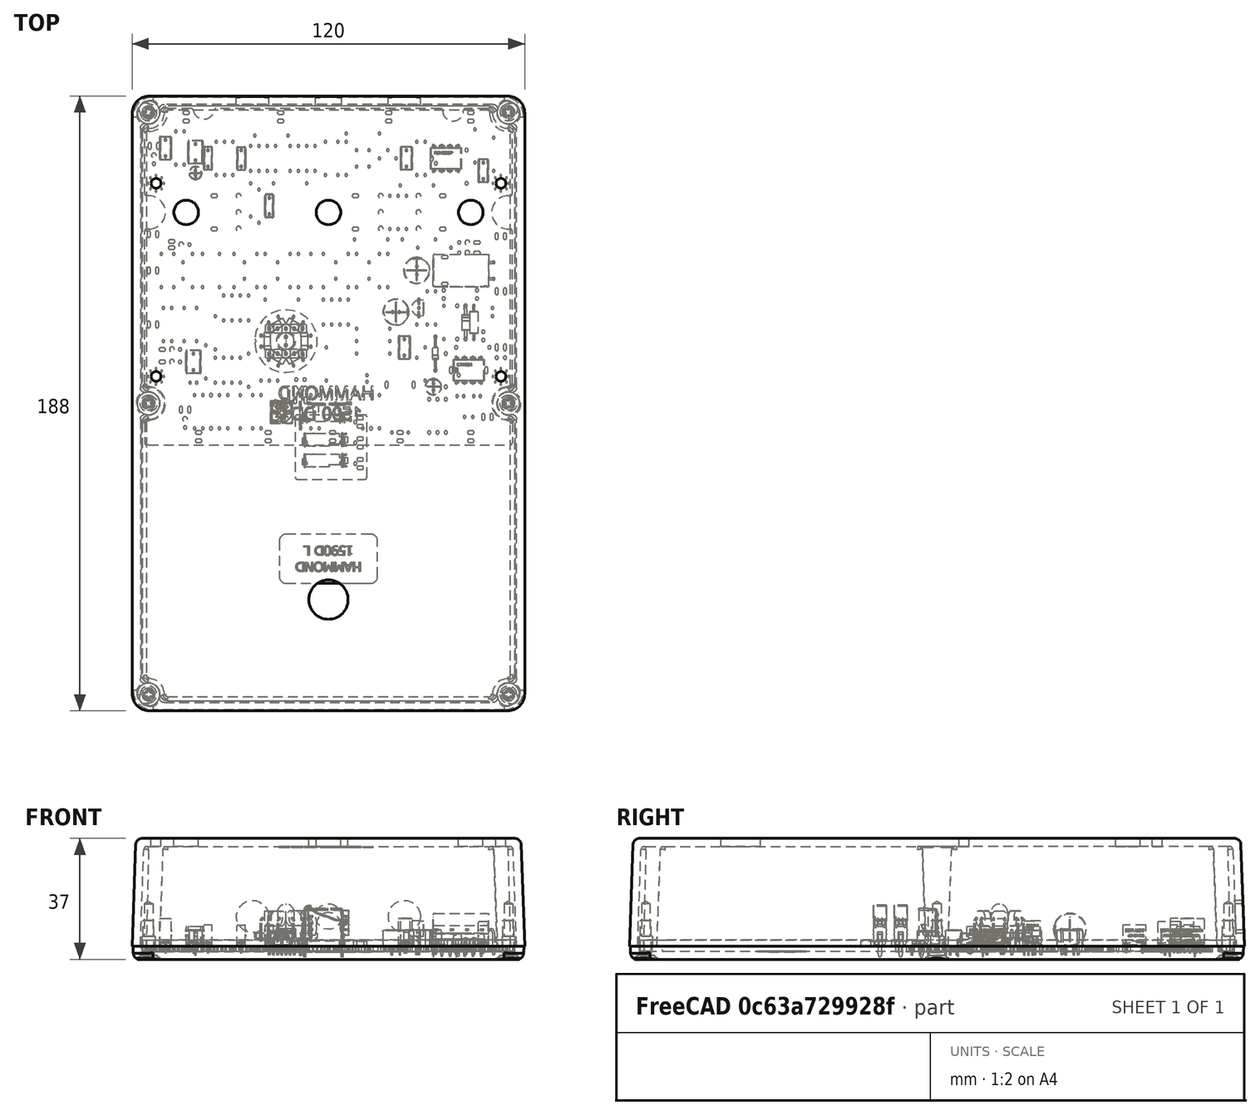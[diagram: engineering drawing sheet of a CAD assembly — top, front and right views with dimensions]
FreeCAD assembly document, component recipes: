
FREECAD ASSEMBLY — COMPONENT RECIPES ("#000-000 - Mu-Tron Phasor II - ASM3")

This assembly document has 7 components, labeled P0..P6 below (a component is one placed body or linked part). 2 of them carry a construction recipe — the FreeCAD feature program that regenerates the part from scratch, quoted from this document or its linked companion documents; the rest are supplied as boundary geometry only. No exploded tour is included for this assembly.
COMPONENT P0 — geometry summary ("#110-000-S1A - Phasor PCB"; no construction recipe available for this part):
  bounding box: 145.4 x 142.2 x 16.1 mm
  tessellated surface: 227,022 triangles
  volume: 29561 mm^3 (9% of its bounding box)
COMPONENT P1 — recipe-attached ("Hex_Spacer_FF_M3x12_FF4.008", modeled in this document).
Construction recipe (the document's own serialized feature program — sketch geometry with constraints, then the solid features built on it; lengths are millimeters unless a unit is written):

FEATURE [Sketcher::SketchObject] Sketch
  MapMode = 5
  Support = -> [XY_Plane005]
  sketch-geometry (7):
    g0: LineSegment StartX=2.35 StartY=1.35677 StartZ=0 EndX=0 EndY=2.71355 EndZ=0
    g1: LineSegment StartX=0 StartY=2.71355 StartZ=0 EndX=-2.35 EndY=1.35677 EndZ=0
    g2: LineSegment StartX=-2.35 StartY=1.35677 StartZ=0 EndX=-2.35 EndY=-1.35677 EndZ=0
    g3: LineSegment StartX=-2.35 StartY=-1.35677 StartZ=0 EndX=-2.2e-15 EndY=-2.71355 EndZ=0
    g4: LineSegment StartX=-2.2e-15 StartY=-2.71355 StartZ=0 EndX=2.35 EndY=-1.35677 EndZ=0
    g5: LineSegment StartX=2.35 StartY=-1.35677 StartZ=0 EndX=2.35 EndY=1.35677 EndZ=0
    g6: Circle [constr] CenterX=0 CenterY=0 CenterZ=0 NormalX=0 NormalY=0 NormalZ=1 AngleXU=0 Radius=2.71355
  constraints (16):
    c: Coincident(g0,g1)
    c: Coincident(g1,g2)
    c: Coincident(g2,g3)
    c: Coincident(g3,g4)
    c: Coincident(g4,g5)
    c: Coincident(g5,g0)
    c: Equal(g0, g1-g5) x5
    c: PointOnObject(g0,g6)
    c: PointOnObject(g1,g6)
    c: PointOnObject(g2,g6)
    c: PointOnObject(g3,g6)
    c: PointOnObject(g4,g6)
    c: PointOnObject(g5,g6)
    c: Coincident(g6,g-1)
    c: PointOnObject(g0,g-2)
    c: DistanceX(g1,g0) = 4.7
FEATURE [PartDesign::Pad] Pad
  ClaimChildren = false
  Length = 12
  Length2 = 100
  Profile = -> Sketch
  Type = 0
FEATURE [Sketcher::SketchObject] Sketch001
  MapMode = 5
  Placement = pos=(0,0,0) rot=(1,0,0;3.14159rad)
  Support = -> [Pad]
  sketch-geometry (1):
    g0: Circle CenterX=0 CenterY=0 CenterZ=0 NormalX=0 NormalY=0 NormalZ=1 AngleXU=0 Radius=1.5
  constraints (2):
    c: Coincident(g0,g-1)
    c: Radius(g0) = 1.5
FEATURE [PartDesign::Pocket] Pocket
  BaseFeature = -> Pad
  ClaimChildren = false
  Length = 5
  Length2 = 100
  Profile = -> Sketch001
  Type = 1
FEATURE [PartDesign::Body] Body001  label="Hex_Spacer_FF_M3x12_FF4.7"
  Group = -> [Sketch,Pad,Sketch001,Pocket]
  Origin = -> Origin005
  Tip = -> Pocket
COMPONENT P2 — recipe-attached ("Screw_M3x6_T_2.0_Panhead001", modeled in this document).
Construction recipe (the document's own serialized feature program — sketch geometry with constraints, then the solid features built on it; lengths are millimeters unless a unit is written):

FEATURE [Sketcher::SketchObject] Sketch002
  MapMode = 5
  Placement = pos=(0,0,0) rot=(1,0,0;1.5708rad)
  Support = -> [XZ_Plane006]
  sketch-geometry (11):
    g0: LineSegment StartX=0 StartY=-6 StartZ=0 EndX=-1.4 EndY=-6 EndZ=0
    g1: LineSegment StartX=-1.4 StartY=-6 StartZ=0 EndX=-1.4 EndY=0 EndZ=0
    g2: LineSegment StartX=-1.4 StartY=0 StartZ=0 EndX=-2.9 EndY=0 EndZ=0
    g3: LineSegment StartX=-2.9 StartY=0 StartZ=0 EndX=-2.9 EndY=1.5 EndZ=0
    g4: LineSegment StartX=0 StartY=-6 StartZ=0 EndX=0 EndY=2 EndZ=0
    g5: Circle [constr] CenterX=0 CenterY=2 CenterZ=0 NormalX=0 NormalY=0 NormalZ=1 AngleXU=0 Radius=0.3
    g6: Circle [constr] CenterX=-1.27 CenterY=2.02886 CenterZ=0 NormalX=0 NormalY=0 NormalZ=1 AngleXU=0 Radius=0.3
    g7: Circle [constr] CenterX=-2.9 CenterY=1.5 CenterZ=0 NormalX=0 NormalY=0 NormalZ=1 AngleXU=0 Radius=0.3
    g8: BSplineCurve PolesCount=3 KnotsCount=2 Degree=2 IsPeriodic=0
    g9: GeomPoint [constr] X=0 Y=2 Z=0
    g10: GeomPoint [constr] X=-2.9 Y=1.5 Z=0
  constraints (26):
    c: PointOnObject(g0,g-2)
    c: Horizontal(g0)
    c: Coincident(g0,g1)
    c: PointOnObject(g1,g-1)
    c: Vertical(g1)
    c: Coincident(g1,g2)
    c: PointOnObject(g2,g-1)
    c: Coincident(g2,g3)
    c: Vertical(g3)
    c: Coincident(g0,g4)
    c: PointOnObject(g4,g-2)
    c: DistanceX(g0,g0) = 1.4
    c: DistanceX(g2,g-1) = 2.9
    c: DistanceY(g3,g3) = 1.5
    c: DistanceY(g-1,g4) = 2
    c: DistanceY(g0,g-1) = 6
    c: Coincident(g8,g4)
    c: Radius(g5) = 0.3
    c: Equal(g5,g6)
    c: Equal(g5,g7)
    c: Coincident(g8,g3)
    c: InternalAlignment(g5,g8)
    c: InternalAlignment(g6,g8)
    c: InternalAlignment(g7,g8)
    c: InternalAlignment(g9,g8)
    c: InternalAlignment(g10,g8)
FEATURE [PartDesign::Revolution] Revolution
  Angle = 360
  Axis = (0,-2e-16,1)
  Base = (0,0,0)
  ClaimChildren = false
  Placement = pos=(0,0,0) rot=(1,0,0;1.5708rad)
  Profile = -> Sketch002
  ReferenceAxis = -> Sketch002 [V_Axis]
FEATURE [Sketcher::SketchObject] Sketch003
  AttachmentOffset = pos=(0,0,1) rot=(0,0,1;0rad)
  MapMode = 5
  Placement = pos=(0,0,1) rot=(0,0,1;0rad)
  Support = -> [XY_Plane006]
  sketch-geometry (12):
    g0: LineSegment StartX=0.375 StartY=1.5 StartZ=0 EndX=-0.375 EndY=1.5 EndZ=0
    g1: LineSegment StartX=-0.375 StartY=1.5 StartZ=0 EndX=-0.375 EndY=0.375 EndZ=0
    g2: LineSegment StartX=-0.375 StartY=0.375 StartZ=0 EndX=-1.5 EndY=0.375 EndZ=0
    g3: LineSegment StartX=-1.5 StartY=0.375 StartZ=0 EndX=-1.5 EndY=-0.375 EndZ=0
    g4: LineSegment StartX=-1.5 StartY=-0.375 StartZ=0 EndX=-0.375 EndY=-0.375 EndZ=0
    g5: LineSegment StartX=-0.375 StartY=-0.375 StartZ=0 EndX=-0.375 EndY=-1.5 EndZ=0
    g6: LineSegment StartX=-0.375 StartY=-1.5 StartZ=0 EndX=0.375 EndY=-1.5 EndZ=0
    g7: LineSegment StartX=0.375 StartY=-1.5 StartZ=0 EndX=0.375 EndY=-0.375 EndZ=0
    g8: LineSegment StartX=0.375 StartY=-0.375 StartZ=0 EndX=1.5 EndY=-0.375 EndZ=0
    g9: LineSegment StartX=1.5 StartY=-0.375 StartZ=0 EndX=1.5 EndY=0.375 EndZ=0
    g10: LineSegment StartX=1.5 StartY=0.375 StartZ=0 EndX=0.375 EndY=0.375 EndZ=0
    g11: LineSegment StartX=0.375 StartY=0.375 StartZ=0 EndX=0.375 EndY=1.5 EndZ=0
  constraints (32):
    c: Coincident(g0,g1)
    c: Vertical(g1)
    c: Coincident(g1,g2)
    c: Horizontal(g2)
    c: Coincident(g2,g3)
    c: Vertical(g3)
    c: Coincident(g3,g4)
    c: Horizontal(g4)
    c: Coincident(g4,g5)
    c: Coincident(g5,g6)
    c: Horizontal(g6)
    c: Coincident(g6,g7)
    c: Coincident(g7,g8)
    c: Horizontal(g8)
    c: Coincident(g8,g9)
    c: Coincident(g9,g10)
    c: Horizontal(g10)
    c: Coincident(g10,g11)
    c: Coincident(g11,g0)
    c: Vertical(g7)
    c: Symmetric(g0,g0,g-2)
    c: Symmetric(g9,g8,g-1)
    c: Equal(g0,g6)
    c: Equal(g9,g3)
    c: Equal(g10,g2)
    c: DistanceX(g2,g9) = 3
    c: Equal(g2,g4)
    c: DistanceY(g6,g0) = 3
    c: Symmetric(g0,g6,g-1)
    c: Symmetric(g9,g2,g-2)
    c: DistanceX(g0,g0) = 0.75
    c: DistanceY(g9,g9) = 0.75
FEATURE [PartDesign::Pocket] Pocket001
  BaseFeature = -> Revolution
  ClaimChildren = false
  Length = 5
  Length2 = 100
  Placement = pos=(0,0,0) rot=(1,0,0;1.5708rad)
  Profile = -> Sketch003
  Reversed = true
  Type = 1
FEATURE [PartDesign::Body] Body002  label="Screw_M3x6_T_2.0_Panhead"
  Group = -> [Sketch002,Revolution,Sketch003,Pocket001]
  Origin = -> Origin006
  Placement = pos=(0,99,51) rot=(0,0,1;0rad)
  SingleSolid = true
  Tip = -> Pocket001
COMPONENT P3 — geometry summary ("#500-000-A1 - Audio Jack PCBA [Input, Pads L] - STEP"; no construction recipe available for this part):
  bounding box: 28.5 x 28.4 x 15.9 mm
  tessellated surface: 5,432 triangles
  volume: 2986 mm^3 (23% of its bounding box)
COMPONENT P4 — geometry summary ("#700-000-A - Enclosure [1590DD, Portrait]"; no construction recipe available for this part):
  bounding box: 219.1 x 196.3 x 33.0 mm
  tessellated surface: 51,366 triangles
  volume: 104393 mm^3 (7% of its bounding box)
  symmetry: 2-fold rotationally symmetric about the z axis
COMPONENT P5 — geometry summary ("RV54_Alpha_RV16AF-41-15R-XXX_5DC04847"; no construction recipe available for this part):
  bounding box: 30.7 x 25.9 x 22.7 mm
  tessellated surface: 13,738 triangles
  volume: 1291 mm^3 (7% of its bounding box)
COMPONENT P6 — geometry summary ("RV53_Alpha_RV16AF-41-15R-XXX_5DF1A8EF"; no construction recipe available for this part):
  bounding box: 30.7 x 25.9 x 22.5 mm
  tessellated surface: 13,738 triangles
  volume: 1291 mm^3 (7% of its bounding box)
PROVENANCE & LICENSES
A FreeCAD (.FCStd) document from a public repository crawl; recipes are the document's own serialized feature recipes (and, for linked parts, companion documents' recipes).
License: as declared in the source repository (recorded in the dataset sidecar).
